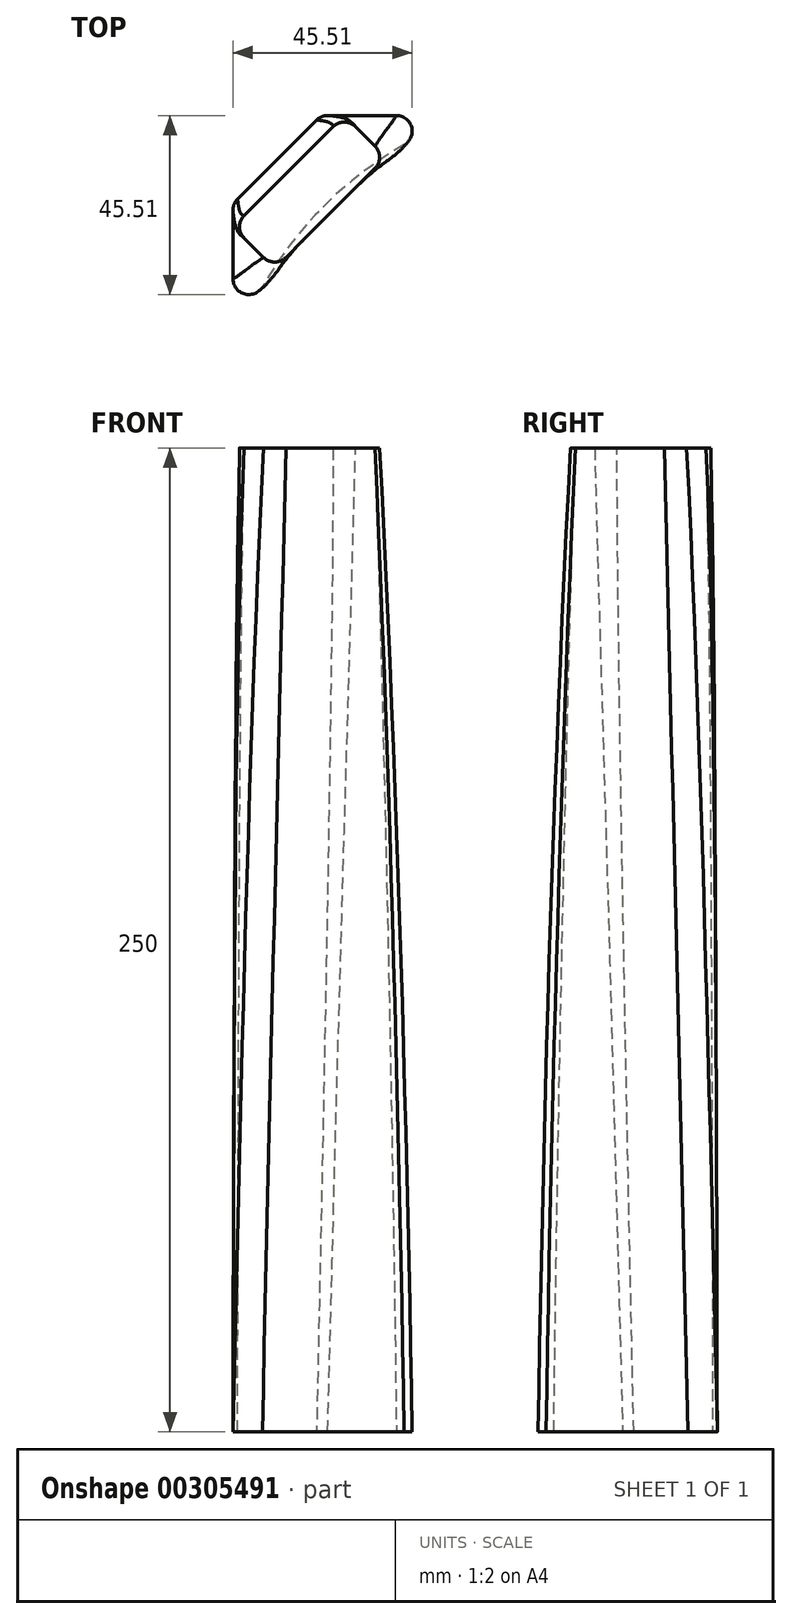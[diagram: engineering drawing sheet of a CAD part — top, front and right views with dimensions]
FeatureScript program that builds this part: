
annotation { "Feature Type Name" : "Feature", "Feature Type Description" : "" }
export const myFeature = defineFeature(function(context is Context, id is Id, definition is map)
    precondition{}
    {
        {
            var Q0;
            Q0=qCreatedBy(makeId("Top.planeOp"),FACE);
            var sketch = newSketch(context, id + "F0", { "sketchPlane" : qUnion([Q0])});
            skLineSegment(sketch, "E0.bottom", {"start": v(0, 0) * mm, "end": v(60, 0) * mm});
            skLineSegment(sketch, "E0.left", {"start": v(0, -15) * mm, "end": v(0, -60) * mm});
            skArc(sketch, "E1", {"start": v(0, -15) * mm, "mid": v(9.72, -9.72) * mm, "end": v(15, 0) * mm, "construction": true});
            skArc(sketch, "E2", {"start": v(60, 0) * mm, "mid": v(23.07, -23.07) * mm, "end": v(0, -60) * mm});
            skLineSegment(sketch, "E3", {"start": v(-4.06, 4.06) * mm, "end": v(91.48, -91.48) * mm, "construction": true});
            skLineSegment(sketch, "E4", {"start": v(22.39, 0) * mm, "end": v(0, -22.39) * mm});
            skSolve(sketch);
        }
        {
            var Q0;
            Q0=qCreatedBy(makeId("Top.planeOp"),FACE);
            cPlane(context, id + "F1", {"entities" : qUnion([Q0]), "cplaneType" : CPlaneType.OFFSET, "offset" : 250 * mm, "width" : 150 * mm, "height" : 150 * mm});
        }
        {
            var Q0;
            Q0=qCreatedBy(id+"F1.planeOp",FACE);
            var sketch = newSketch(context, id + "F2", { "sketchPlane" : qUnion([Q0])});
            skLineSegment(sketch, "E5", {"start": v(28.28, 0) * mm, "end": v(0, -28.28) * mm});
            skLineSegment(sketch, "E6", {"start": v(0, -28.28) * mm, "end": v(10.6, -38.9) * mm});
            skLineSegment(sketch, "E7", {"start": v(10.6, -38.9) * mm, "end": v(38.9, -10.6) * mm});
            skLineSegment(sketch, "E8", {"start": v(38.9, -10.6) * mm, "end": v(28.28, 0) * mm});
            skSolve(sketch);
        }
        {
            var Q0;
            Q0=makeQuery(id+"F2.imprint","IMPRINT",FACE,{"disambiguationData":[TD([[makeQuery(id+"F2.imprint","IMPRINT",EDGE,{"derivedFrom":sQuery(id+"F2.wireOp",EDGE,"E5")}),1.0]])]});
            var Q1;
            Q1=makeQuery(id+"F0.imprint","IMPRINT",FACE,{"disambiguationData":[TD([[makeQuery(id+"F0.imprint","IMPRINT",EDGE,{"derivedFrom":sQuery(id+"F0.wireOp",EDGE,"E0.left")}),1.0]])]});
            loft(context, id + "F3", {"sheetProfilesArray" : [{ "sheetProfileEntities" : qUnion([Q0]) }, { "sheetProfileEntities" : qUnion([Q1]) }]});
        }
        {
            var Q0;
            Q0=makeQuery(id+"F3.opLoft","SWEPT_EDGE",EDGE,{"disambiguationData":[OSD([sQuery(id+"F0.wireOp",EDGE,"E0.left"),sQuery(id+"F0.wireOp",EDGE,"E2"),sQuery(id+"F2.wireOp",EDGE,"E6"),sQuery(id+"F2.wireOp",EDGE,"E7")])]});
            var Q1;
            Q1=makeQuery(id+"F3.opLoft","SWEPT_EDGE",EDGE,{"disambiguationData":[OSD([sQuery(id+"F0.wireOp",EDGE,"E0.bottom"),sQuery(id+"F0.wireOp",EDGE,"E2"),sQuery(id+"F2.wireOp",EDGE,"E7"),sQuery(id+"F2.wireOp",EDGE,"E8")])]});
            var Q2;
            Q2=makeQuery(id+"F3.opLoft","SWEPT_EDGE",EDGE,{"disambiguationData":[OSD([sQuery(id+"F0.wireOp",EDGE,"E0.bottom"),sQuery(id+"F0.wireOp",EDGE,"E1"),sQuery(id+"F2.wireOp",EDGE,"E5"),sQuery(id+"F2.wireOp",EDGE,"E8")])]});
            var Q3;
            Q3=makeQuery(id+"F3.opLoft","SWEPT_EDGE",EDGE,{"disambiguationData":[OSD([sQuery(id+"F0.wireOp",EDGE,"E0.left"),sQuery(id+"F0.wireOp",EDGE,"E1"),sQuery(id+"F2.wireOp",EDGE,"E5"),sQuery(id+"F2.wireOp",EDGE,"E6")])]});
            fillet(context, id + "F4", {"entities" : qUnion([Q0, Q1, Q2, Q3]), "radius" : 4 * mm, "tangentPropagation" : true, "allowEdgeOverflow" : false});
        }
    });
